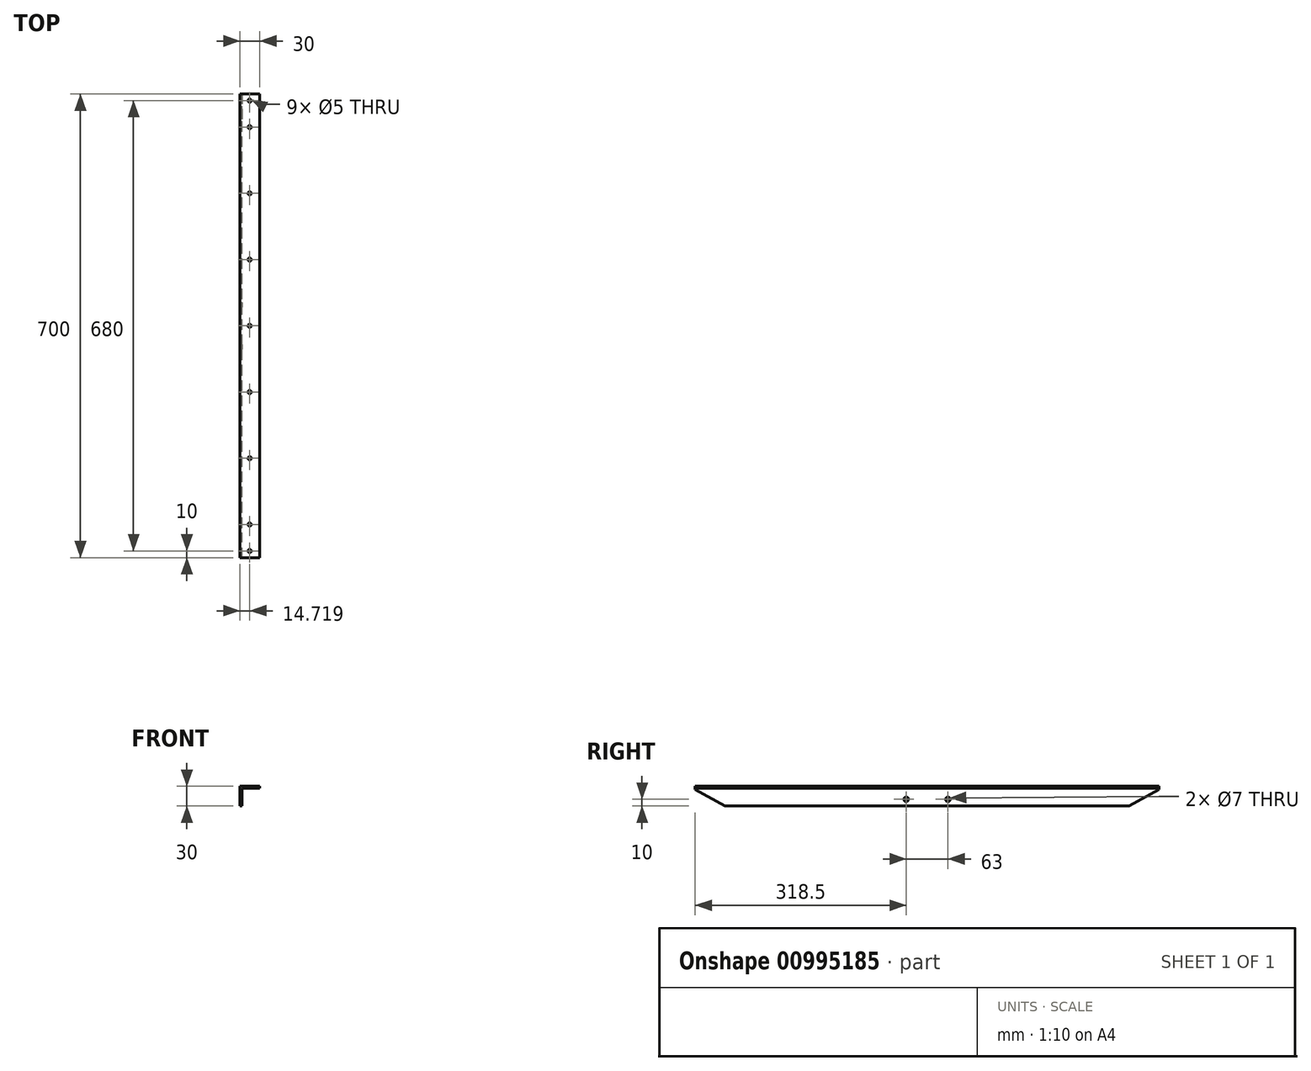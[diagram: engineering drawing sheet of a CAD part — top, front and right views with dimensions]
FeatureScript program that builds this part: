
annotation { "Feature Type Name" : "Feature", "Feature Type Description" : "" }
export const myFeature = defineFeature(function(context is Context, id is Id, definition is map)
    precondition{}
    {
        {
            var Q0;
            Q0=qCreatedBy(makeId("Front.planeOp"),FACE);
            var sketch = newSketch(context, id + "F0", { "sketchPlane" : qUnion([Q0])});
            skLineSegment(sketch, "E0", {"start": v(0, 0) * mm, "end": v(0, 30) * mm});
            skLineSegment(sketch, "E1", {"start": v(0, 30) * mm, "end": v(30, 30) * mm});
            skLineSegment(sketch, "E2", {"start": v(30, 30) * mm, "end": v(30, 27) * mm});
            skLineSegment(sketch, "E3", {"start": v(30, 27) * mm, "end": v(3, 27) * mm});
            skLineSegment(sketch, "E4", {"start": v(3, 27) * mm, "end": v(3, 0) * mm});
            skLineSegment(sketch, "E5", {"start": v(3, 0) * mm, "end": v(0, 0) * mm});
            skSolve(sketch);
        }
        {
            var Q0;
            Q0=makeQuery(id+"F0.imprint","IMPRINT",FACE,{"disambiguationData":[TD([[makeQuery(id+"F0.imprint","IMPRINT",EDGE,{"derivedFrom":sQuery(id+"F0.wireOp",EDGE,"E0")}),-1.0]])]});
            extrude(context, id + "F1", {"entities" : qUnion([Q0]), "depth" : 700 * mm, "offsetDistance" : 25 * mm, "symmetric" : true});
        }
        {
            var Q0;
            Q0=makeQuery(id+"F1.opExtrude","SWEPT_FACE",FACE,{"disambiguationData":[OSD([sQuery(id+"F0.wireOp",EDGE,"E0")])]});
            var sketch = newSketch(context, id + "F2", { "sketchPlane" : qUnion([Q0])});
            skLineSegment(sketch, "E6", {"start": v(0, 30) * mm, "end": v(0, 10) * mm});
            skLineSegment(sketch, "E7", {"start": v(0, 10) * mm, "end": v(-31.5, 10) * mm});
            skLineSegment(sketch, "E8", {"start": v(0, 10) * mm, "end": v(31.5, 10) * mm});
            skSolve(sketch);
        }
        {
            var Q0;
            Q0=sQuery(id+"F2.wireOp",VERTEX,"E7.end");
            var Q1;
            Q1=sQuery(id+"F2.wireOp",VERTEX,"E8.end");
            var Q2;
            Q2=makeQuery(id+"F1.opExtrude","SWEPT_BODY",BODY,{"disambiguationData":[OSD([sQuery(id+"F0.wireOp",EDGE,"E0"),sQuery(id+"F0.wireOp",EDGE,"E1"),sQuery(id+"F0.wireOp",EDGE,"E2"),sQuery(id+"F0.wireOp",EDGE,"E3"),sQuery(id+"F0.wireOp",EDGE,"E4"),sQuery(id+"F0.wireOp",EDGE,"E5")])]});
            hole(context, id + "F3", {"style" : HoleStyle.SIMPLE, "endStyle" : HoleEndStyle.THROUGH, "holeDiameter" : 7 * mm, "majorDiameter" : 5 * mm, "isTappedThrough" : true, "tappedDepth" : 12 * mm, "tapClearance" : 3, "locations" : qUnion([Q0, Q1]), "scope" : qUnion([Q2]), "startStyle" : HoleStartStyle.PART});
        }
        {
            var Q0;
            Q0=makeQuery(id+"F1.opExtrude","SWEPT_FACE",FACE,{"disambiguationData":[OSD([sQuery(id+"F0.wireOp",EDGE,"E1")])]});
            var sketch = newSketch(context, id + "F4", { "sketchPlane" : qUnion([Q0])});
            skLineSegment(sketch, "E9", {"start": v(0, 0) * mm, "end": v(14.72, 0) * mm});
            skLineSegment(sketch, "E10", {"start": v(14.72, 0) * mm, "end": v(14.72, 100) * mm});
            skLineSegment(sketch, "E11", {"start": v(14.72, 100) * mm, "end": v(14.72, 200) * mm});
            skLineSegment(sketch, "E12", {"start": v(14.72, 200) * mm, "end": v(14.72, 300) * mm});
            skLineSegment(sketch, "E13", {"start": v(14.72, 0) * mm, "end": v(14.72, -100) * mm});
            skLineSegment(sketch, "E14", {"start": v(14.72, -100) * mm, "end": v(14.72, -200) * mm});
            skLineSegment(sketch, "E15", {"start": v(14.72, -200) * mm, "end": v(14.72, -300) * mm});
            skLineSegment(sketch, "E16", {"start": v(14.72, -300) * mm, "end": v(14.72, -340) * mm});
            skLineSegment(sketch, "E17", {"start": v(14.72, 300) * mm, "end": v(14.72, 340) * mm});
            skSolve(sketch);
        }
        {
            var Q0;
            Q0=sQuery(id+"F4.wireOp",VERTEX,"E12.end");
            var Q1;
            Q1=sQuery(id+"F4.wireOp",VERTEX,"E12.start");
            var Q2;
            Q2=sQuery(id+"F4.wireOp",VERTEX,"E11.start");
            var Q3;
            Q3=sQuery(id+"F4.wireOp",VERTEX,"E13.start");
            var Q4;
            Q4=sQuery(id+"F4.wireOp",VERTEX,"E14.start");
            var Q5;
            Q5=sQuery(id+"F4.wireOp",VERTEX,"E15.start");
            var Q6;
            Q6=sQuery(id+"F4.wireOp",VERTEX,"E15.end");
            var Q7;
            Q7=sQuery(id+"F4.wireOp",VERTEX,"gbc2nK7E-ztz0-IBhr-DfQU-EQeF7ijxsCjM.end");
            var Q8;
            Q8=sQuery(id+"F4.wireOp",VERTEX,"ZtBBAAtL-lso0-mhiq-NLzV-Yrly4486QW8c.end");
            var Q9;
            Q9=sQuery(id+"F4.wireOp",VERTEX,"E16.end");
            var Q10;
            Q10=sQuery(id+"F4.wireOp",VERTEX,"E17.end");
            var Q11;
            Q11=makeQuery(id+"F1.opExtrude","SWEPT_BODY",BODY,{"disambiguationData":[OSD([sQuery(id+"F0.wireOp",EDGE,"E0"),sQuery(id+"F0.wireOp",EDGE,"E1"),sQuery(id+"F0.wireOp",EDGE,"E2"),sQuery(id+"F0.wireOp",EDGE,"E3"),sQuery(id+"F0.wireOp",EDGE,"E4"),sQuery(id+"F0.wireOp",EDGE,"E5")])]});
            hole(context, id + "F5", {"style" : HoleStyle.SIMPLE, "endStyle" : HoleEndStyle.THROUGH, "holeDiameter" : 5 * mm, "majorDiameter" : 5 * mm, "isTappedThrough" : true, "tappedDepth" : 12 * mm, "tapClearance" : 3, "locations" : qUnion([Q0, Q1, Q2, Q3, Q4, Q5, Q6, Q7, Q8, Q9, Q10]), "scope" : qUnion([Q11]), "startStyle" : HoleStartStyle.PART});
        }
        {
            var Q0;
            Q0=makeQuery(id+"F1.opExtrude","SWEPT_FACE",FACE,{"disambiguationData":[OSD([sQuery(id+"F0.wireOp",EDGE,"E0")])]});
            var sketch = newSketch(context, id + "F6", { "sketchPlane" : qUnion([Q0])});
            skLineSegment(sketch, "E18", {"start": v(-350, 25) * mm, "end": v(-350, 0) * mm});
            skLineSegment(sketch, "E19", {"start": v(-350, 0) * mm, "end": v(-305, 0) * mm});
            skLineSegment(sketch, "E20", {"start": v(-305, 0) * mm, "end": v(-350, 25) * mm});
            skLineSegment(sketch, "E21", {"start": v(350, 25) * mm, "end": v(350, 0) * mm});
            skLineSegment(sketch, "E22", {"start": v(350, 0) * mm, "end": v(305, 0) * mm});
            skLineSegment(sketch, "E23", {"start": v(305, 0) * mm, "end": v(350, 25) * mm});
            skSolve(sketch);
        }
        {
            var Q0;
            Q0=qSketchRegion(id+"F6",true);
            extrude(context, id + "F7", {"entities" : qUnion([Q0]), "operationType" : NewBodyOperationType.REMOVE, "oppositeDirection" : true, "depth" : 25 * mm, "offsetDistance" : 25 * mm});
        }
    });
